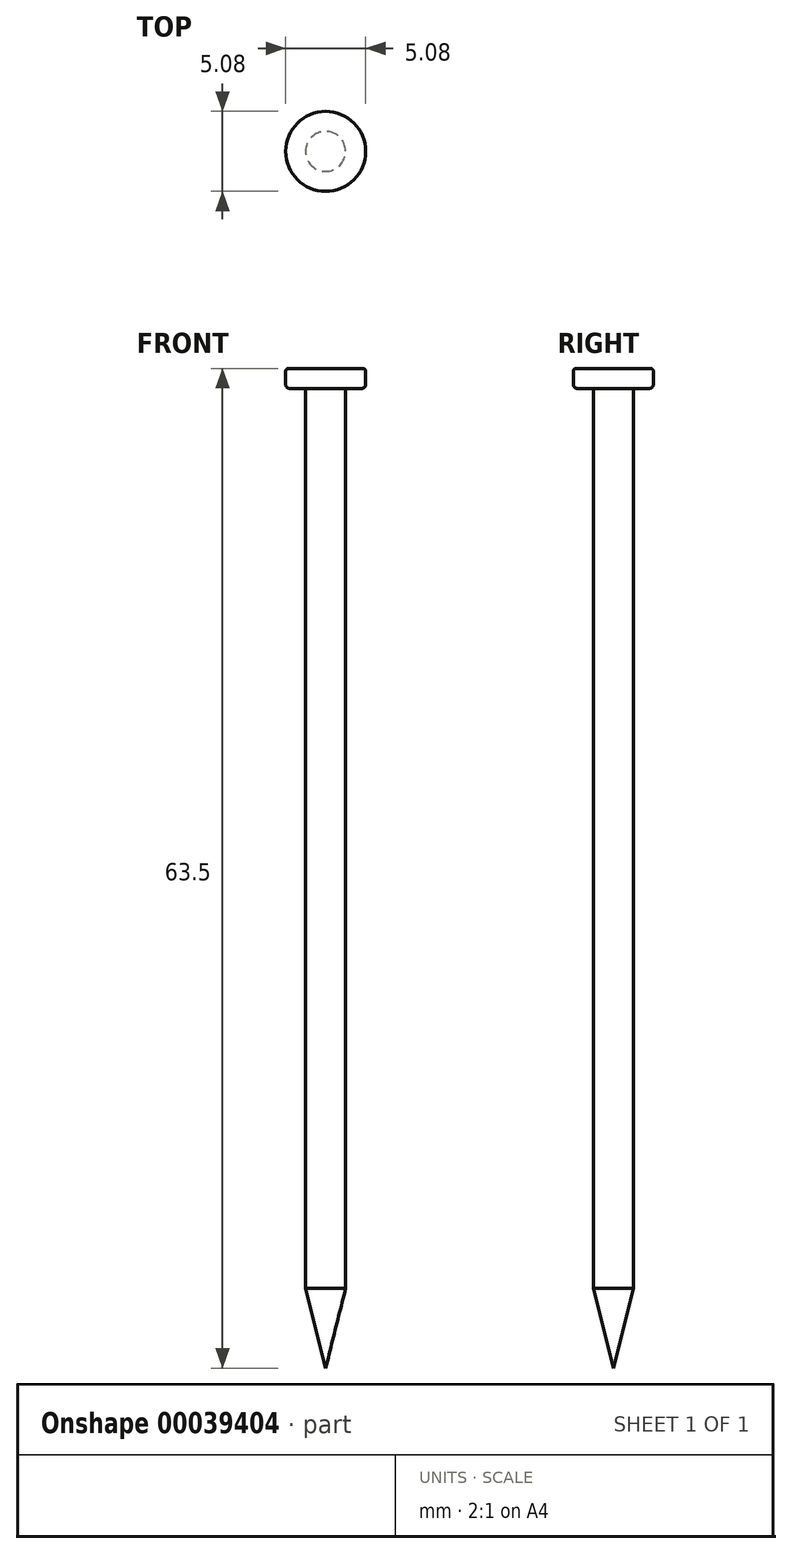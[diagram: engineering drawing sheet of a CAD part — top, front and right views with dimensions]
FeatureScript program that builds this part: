
annotation { "Feature Type Name" : "Feature", "Feature Type Description" : "" }
export const myFeature = defineFeature(function(context is Context, id is Id, definition is map)
    precondition{}
    {
        {
            var Q0;
            Q0=qCreatedBy(makeId("Front.planeOp"),FACE);
            var sketch = newSketch(context, id + "F0", { "sketchPlane" : qUnion([Q0])});
            skLineSegment(sketch, "E0", {"start": v(0, 30.07) * mm, "end": v(0, -33.43) * mm});
            skLineSegment(sketch, "E1", {"start": v(0, 30.07) * mm, "end": v(2.54, 30.07) * mm});
            skLineSegment(sketch, "E2", {"start": v(2.54, 30.07) * mm, "end": v(2.54, 28.8) * mm});
            skLineSegment(sketch, "E3", {"start": v(2.54, 28.8) * mm, "end": v(1.27, 28.8) * mm});
            skLineSegment(sketch, "E4", {"start": v(1.27, 28.8) * mm, "end": v(1.27, -28.35) * mm});
            skLineSegment(sketch, "E5", {"start": v(1.27, -28.35) * mm, "end": v(0, -33.43) * mm});
            skSolve(sketch);
        }
        {
            var Q0;
            Q0=makeQuery(id+"F0.imprint","IMPRINT",FACE,{"disambiguationData":[TD([[makeQuery(id+"F0.imprint","IMPRINT",EDGE,{"derivedFrom":sQuery(id+"F0.wireOp",EDGE,"E0")}),1.0]])]});
            var Q1;
            Q1=sQuery(id+"F0.wireOp",EDGE,"E0");
            revolve(context, id + "F1", {"entities" : qUnion([Q0]), "axis" : qUnion([Q1]), "revolveType" : RevolveType.FULL});
        }
        {
            var Q0;
            Q0=makeQuery(id+"F1.opRevolve","SWEPT_EDGE",EDGE,{"disambiguationData":[OSD([sQuery(id+"F0.wireOp",EDGE,"E2"),sQuery(id+"F0.wireOp",EDGE,"E3")])]});
            fillet(context, id + "F2", {"entities" : qUnion([Q0]), "radius" : 0.25 * mm, "tangentPropagation" : true, "allowEdgeOverflow" : false});
        }
        {
            var Q0;
            Q0=makeQuery(id+"F1.opRevolve","SWEPT_EDGE",EDGE,{"disambiguationData":[OSD([sQuery(id+"F0.wireOp",EDGE,"E1"),sQuery(id+"F0.wireOp",EDGE,"E2")])]});
            fillet(context, id + "F3", {"entities" : qUnion([Q0]), "radius" : 0.18 * mm, "tangentPropagation" : true, "allowEdgeOverflow" : false});
        }
    });
